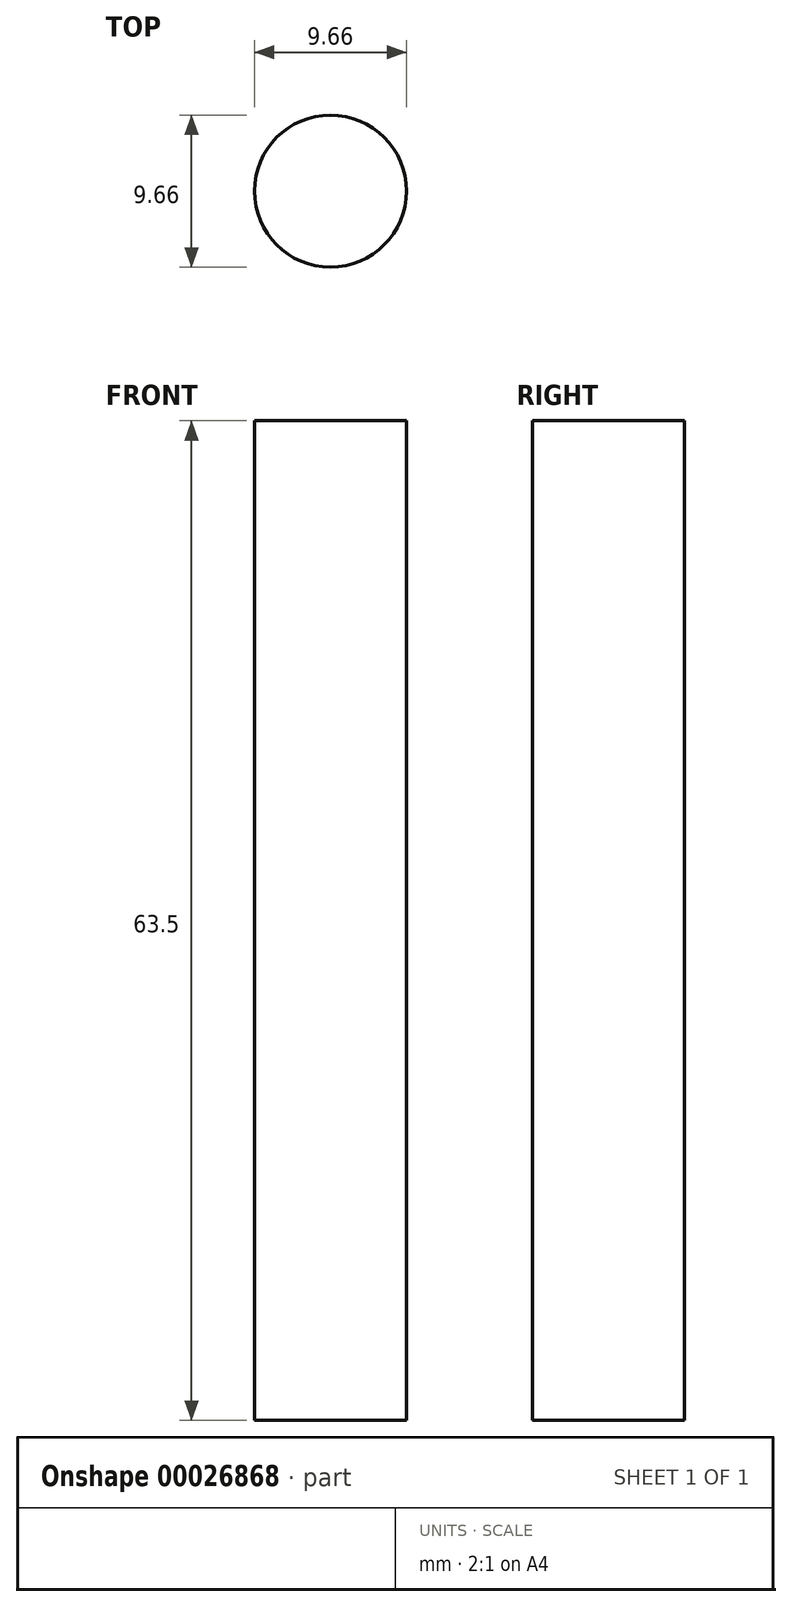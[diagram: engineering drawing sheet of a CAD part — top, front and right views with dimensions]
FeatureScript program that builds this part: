
annotation { "Feature Type Name" : "Feature", "Feature Type Description" : "" }
export const myFeature = defineFeature(function(context is Context, id is Id, definition is map)
    precondition{}
    {
        {
            var Q0;
            Q0=qCreatedBy(makeId("Top.planeOp"),FACE);
            var sketch = newSketch(context, id + "F0", { "sketchPlane" : qUnion([Q0])});
            skCircle(sketch, "E0", {"center": v(0, 0) * mm, "radius": 4.83 * mm});
            skSolve(sketch);
        }
        {
            var Q0;
            Q0=makeQuery(id+"F0.imprint","IMPRINT",FACE,{"disambiguationData":[TD([[makeQuery(id+"F0.imprint","IMPRINT",EDGE,{"derivedFrom":sQuery(id+"F0.wireOp",EDGE,"E0")}),1.0]])]});
            extrude(context, id + "F1", {"entities" : qUnion([Q0]), "depth" : 63.5 * mm});
        }
    });
